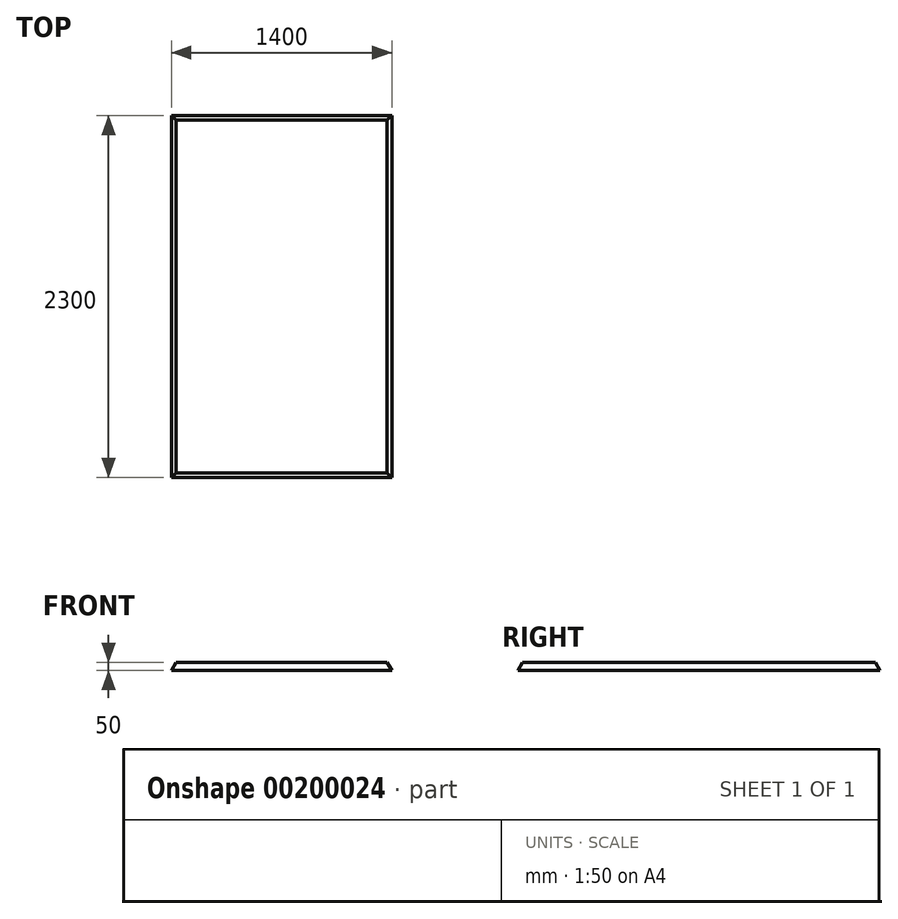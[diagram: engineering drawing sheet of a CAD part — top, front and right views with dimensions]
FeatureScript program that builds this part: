
annotation { "Feature Type Name" : "Feature", "Feature Type Description" : "" }
export const myFeature = defineFeature(function(context is Context, id is Id, definition is map)
    precondition{}
    {
        {
            var Q0;
            Q0=qCreatedBy(makeId("Top.planeOp"),FACE);
            var sketch = newSketch(context, id + "F0", { "sketchPlane" : qUnion([Q0])});
            skLineSegment(sketch, "E0.bottom", {"start": v(-700, 1150) * mm, "end": v(700, 1150) * mm});
            skLineSegment(sketch, "E0.top", {"start": v(-700, -1150) * mm, "end": v(700, -1150) * mm});
            skLineSegment(sketch, "E0.left", {"start": v(-700, 1150) * mm, "end": v(-700, -1150) * mm});
            skLineSegment(sketch, "E0.right", {"start": v(700, 1150) * mm, "end": v(700, -1150) * mm});
            skSolve(sketch);
        }
        {
            var Q0;
            Q0 = qSketchRegion(id + "F0", true);
            extrude(context, id + "F1", {"entities" : qUnion([Q0]), "depth" : 50 * mm});
        }
        {
            var Q0;
            Q0=makeQuery(id+"F1.opExtrude","CAP_EDGE",EDGE,{"disambiguationData":[OSD([sQuery(id+"F0.wireOp",EDGE,"E0.top")])],"isStart":false});
            var Q1;
            Q1=makeQuery(id+"F1.opExtrude","CAP_EDGE",EDGE,{"disambiguationData":[OSD([sQuery(id+"F0.wireOp",EDGE,"E0.right")])],"isStart":false});
            var Q2;
            Q2=makeQuery(id+"F1.opExtrude","CAP_EDGE",EDGE,{"disambiguationData":[OSD([sQuery(id+"F0.wireOp",EDGE,"E0.bottom")])],"isStart":false});
            var Q3;
            Q3=makeQuery(id+"F1.opExtrude","CAP_EDGE",EDGE,{"disambiguationData":[OSD([sQuery(id+"F0.wireOp",EDGE,"E0.left")])],"isStart":false});
            chamfer(context, id + "F2", {"entities" : qUnion([Q0, Q1, Q2, Q3]), "chamferType" : ChamferType.TWO_OFFSETS, "width1" : 30 * mm, "oppositeDirection" : false, "width2" : 50 * mm, "tangentPropagation" : true});
        }
    });
